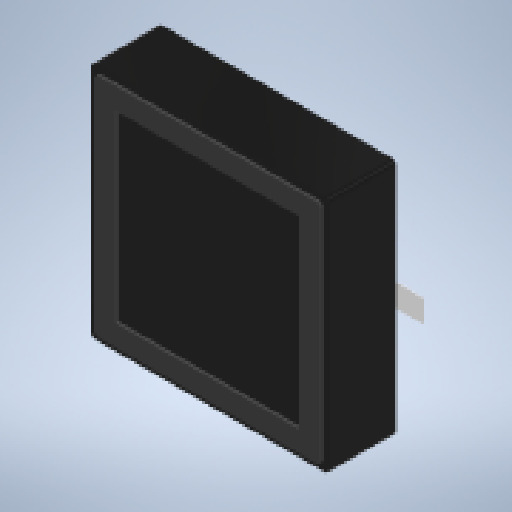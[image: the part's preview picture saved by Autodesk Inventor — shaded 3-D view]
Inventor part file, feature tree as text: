
AUTODESK INVENTOR PART (.ipt)
format: ipt  version: 2024 (Build 280153000, 153)  size: 282,624 bytes
history: native  units: mm
features: extrude x3, sketch x2, fillet x2, projected_geometry x1
ambient origin geometry x8: Origin, YZ Plane, XZ Plane, XY Plane, X Axis, Y Axis, Z Axis, Center Point
bodies: Solid1 (feature_tree)
feature tree (8):
  sketch  "Sketch1"  dims[d0=100.0mm d1=100.0mm]
  extrude  "Extrusion1"  Depth=100.0mm
  extrude  "Extrusion2"  Depth=95.0mm
  fillet  "Fillet1"  Radius=9.0mm
  extrude  "Extrusion3"  Depth=2.0mm
  fillet  "Fillet2"  Radius=28.0mm
  sketch  "Sketch2"  dims[d2=95.0mm d3=95.0mm d4=9.0mm d5=2.0mm d6=28.0mm d7=0.0mm d8=30.5mm d9=0.0mm d10=2.0mm d11=9.5mm d12=22.0mm d13=0.001mm d14=0.2mm d15=0.0mm d16=0.0mm d17=0.5mm d19=0.1mm]
  projected_geometry  "Projected Loop1"
